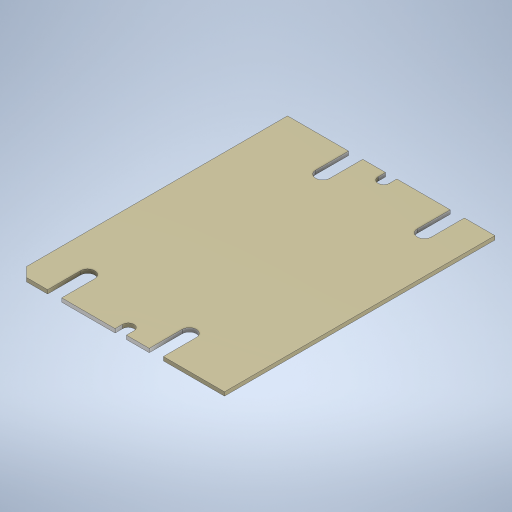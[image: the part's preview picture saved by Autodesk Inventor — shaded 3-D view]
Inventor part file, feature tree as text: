
AUTODESK INVENTOR PART (.ipt)
format: ipt  version: 2023 (Build 270158000, 158)  size: 337,920 bytes
history: native  units: in
note: dims shown in document units (in); Inventor stores cm internally (conversion verified against a paired STEP export)
features: sketch x5, extrude x4, hole x1
ambient origin geometry x8: Origin, YZ Plane, XZ Plane, XY Plane, X Axis, Y Axis, Z Axis, Center Point
bodies: Body1 (feature_tree)
feature tree (10):
  extrude  "Extrusion2"  Depth=2.2638in
  extrude  "Extrusion3"  Depth=0.1181in
  hole  "Hole1"  [1 undecoded]
  extrude  "Extrusion4"  Depth=0.8681in
  extrude  "Extrusion5"  Depth=0.3937in
  sketch  "Sketch2"  dims[d28=1.7362in d29=2.2638in]
  sketch  "Sketch3"  dims[d30=0.0315in d31=0.0in d32=0.1181in]
  sketch  "Sketch4"  dims[d33=0.2756in d34=0.0591in]
  sketch  "Sketch5"  dims[d35=0.0in d36=0.0in d37=0.8681in]
  sketch  "Sketch6"  dims[d38=0.063in d40=0.063in d41=0.0945in d42=0.1575in d43=0.1732in d44=0.0787in d45=0.6181in d46=0.315in d47=0.8108in d48=0.315in d49=0.0787in d50=0.0787in d51=0.0in d52=0.0in d54=1.1657in d60=0.2756in d61=0.2756in d62=0.0591in d63=0.315in d64=0.2756in d65=0.2756in d66=0.0591in d67=1.1657in d68=1.7362in d69=0.3937in d70=0.0in]
note: 1 required parameter value undecoded (feature->parameter linkage not recoverable at this tier; creation-order binding heuristic only, values carry confidence <= 0.55)
